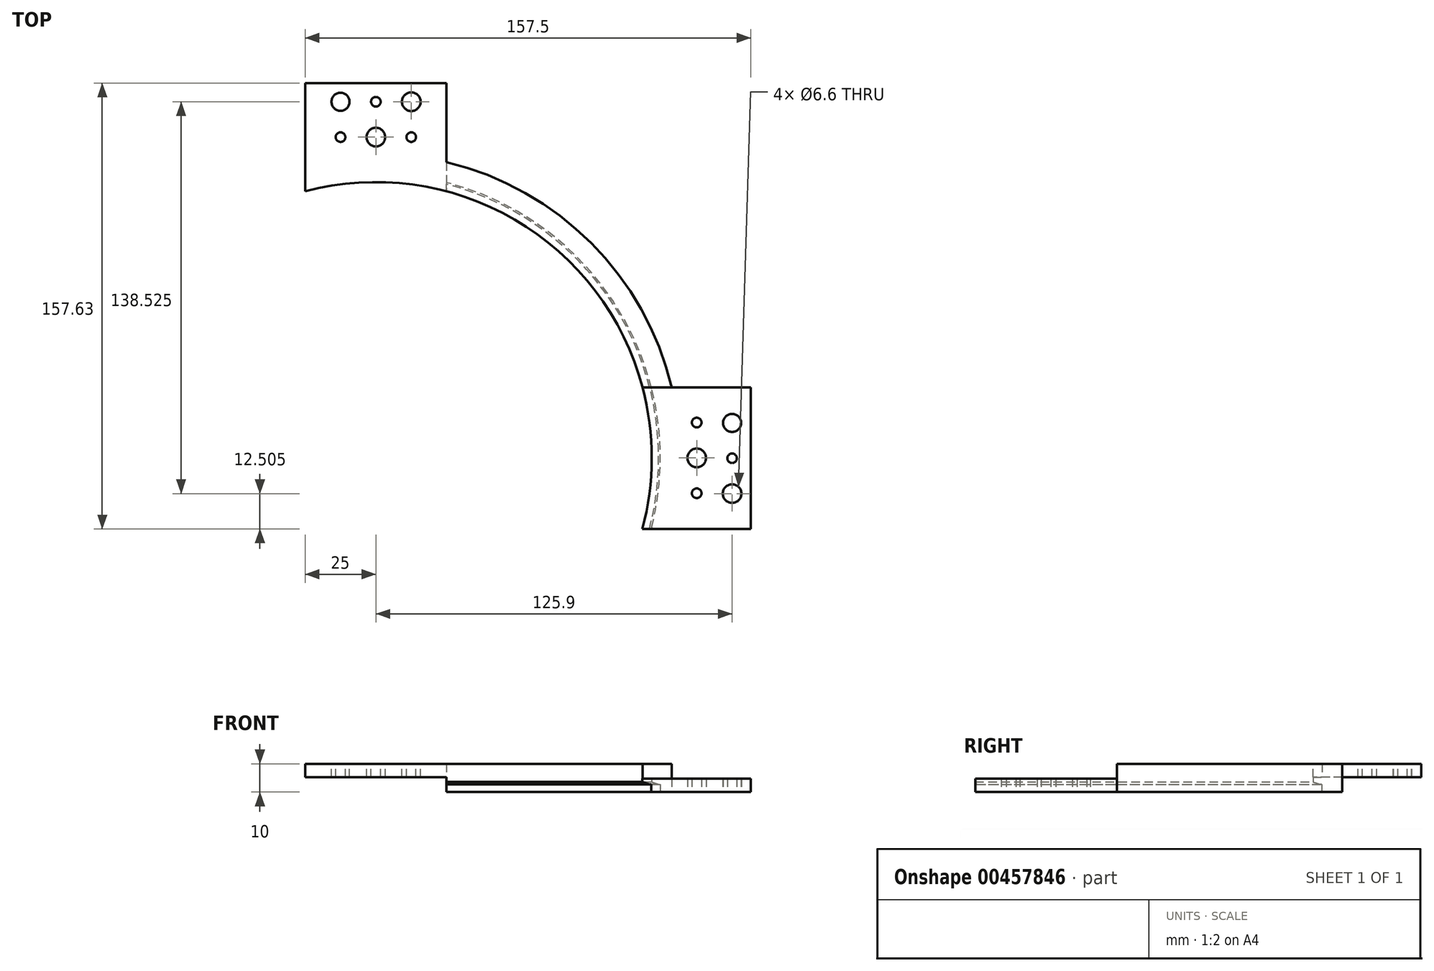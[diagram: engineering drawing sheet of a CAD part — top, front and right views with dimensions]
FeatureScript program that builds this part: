
annotation { "Feature Type Name" : "Feature", "Feature Type Description" : "" }
export const myFeature = defineFeature(function(context is Context, id is Id, definition is map)
    precondition{}
    {
        {
            var Q0;
            Q0=qCreatedBy(makeId("Top.planeOp"),FACE);
            var sketch = newSketch(context, id + "F0", { "sketchPlane" : qUnion([Q0])});
            skCircle(sketch, "E0", {"center": v(0, 0) * mm, "radius": 97.5 * mm});
            skCircle(sketch, "E1", {"center": v(0, 0) * mm, "radius": 107.5 * mm});
            skLineSegment(sketch, "E2", {"start": v(-97.5, 0) * mm, "end": v(-107.5, 0) * mm});
            skLineSegment(sketch, "E3", {"start": v(0, 97.5) * mm, "end": v(0, 107.5) * mm});
            skLineSegment(sketch, "E4", {"start": v(0, -97.5) * mm, "end": v(0, -107.5) * mm});
            skLineSegment(sketch, "E5.bottom", {"start": v(0, 97.5) * mm, "end": v(24.37, 97.5) * mm, "construction": true});
            skLineSegment(sketch, "E5.top", {"start": v(0, 132.5) * mm, "end": v(25, 132.5) * mm, "construction": true});
            skLineSegment(sketch, "E5.left", {"start": v(0, 97.5) * mm, "end": v(0, 132.5) * mm, "construction": true});
            skLineSegment(sketch, "E5.right", {"start": v(25, 97.5) * mm, "end": v(25, 132.5) * mm, "construction": true});
            skLineSegment(sketch, "E6.bottom", {"start": v(0, 132.5) * mm, "end": v(-25, 132.5) * mm, "construction": true});
            skLineSegment(sketch, "E6.top", {"start": v(0, 97.5) * mm, "end": v(-24.37, 97.5) * mm, "construction": true});
            skLineSegment(sketch, "E6.left", {"start": v(0, 132.5) * mm, "end": v(0, 97.5) * mm, "construction": true});
            skLineSegment(sketch, "E6.right", {"start": v(-25, 132.5) * mm, "end": v(-25, 97.5) * mm, "construction": true});
            skLineSegment(sketch, "E7.bottom", {"start": v(-25, 132.5) * mm, "end": v(25, 132.5) * mm});
            skLineSegment(sketch, "E7.top", {"start": v(-24.37, 97.5) * mm, "end": v(24.37, 97.5) * mm});
            skLineSegment(sketch, "E7.left", {"start": v(-25, 132.5) * mm, "end": v(-25, 97.5) * mm});
            skLineSegment(sketch, "E7.right", {"start": v(25, 132.5) * mm, "end": v(25, 97.5) * mm});
            skCircle(sketch, "E8", {"center": v(-12.5, 125.9) * mm, "radius": 3.2 * mm});
            skCircle(sketch, "E9", {"center": v(12.5, 125.9) * mm, "radius": 3.3 * mm});
            skLineSegment(sketch, "E10.top", {"start": v(97.48, -24.43) * mm, "end": v(97.48, -0.13) * mm, "construction": true});
            skLineSegment(sketch, "E11.left", {"start": v(97.48, 0.12) * mm, "end": v(97.48, 24.43) * mm, "construction": true});
            skLineSegment(sketch, "E12", {"start": v(0, 132.5) * mm, "end": v(0, 107.5) * mm});
            skLineSegment(sketch, "E13", {"start": v(-25, 97.5) * mm, "end": v(-25, 94.24) * mm});
            skLineSegment(sketch, "E14", {"start": v(25, 97.5) * mm, "end": v(25, 94.24) * mm});
            skArc(sketch, "E15", {"start": v(24.37, 97.5) * mm, "mid": v(0, 100.5) * mm, "end": v(-24.37, 97.5) * mm});
            skCircle(sketch, "E16", {"center": v(0, 113.4) * mm, "radius": 3.3 * mm});
            skCircle(sketch, "E17", {"center": v(12.5, 113.4) * mm, "radius": 1.7 * mm});
            skCircle(sketch, "E18", {"center": v(-12.5, 113.4) * mm, "radius": 1.7 * mm});
            skLineSegment(sketch, "E19", {"start": v(97.48, -0.13) * mm, "end": v(107.5, -0.13) * mm});
            skLineSegment(sketch, "E20.bottom", {"start": v(97.48, -0.13) * mm, "end": v(97.48, -24.43) * mm, "construction": true});
            skLineSegment(sketch, "E20.top", {"start": v(132.5, -0.13) * mm, "end": v(132.5, -25.13) * mm, "construction": true});
            skLineSegment(sketch, "E20.left", {"start": v(97.48, -0.13) * mm, "end": v(132.5, -0.13) * mm, "construction": true});
            skLineSegment(sketch, "E20.right", {"start": v(97.48, -25.13) * mm, "end": v(132.5, -25.13) * mm, "construction": true});
            skLineSegment(sketch, "E21.bottom", {"start": v(132.5, -0.13) * mm, "end": v(132.5, 24.87) * mm, "construction": true});
            skLineSegment(sketch, "E21.top", {"start": v(97.48, -0.13) * mm, "end": v(97.48, 24.43) * mm, "construction": true});
            skLineSegment(sketch, "E21.left", {"start": v(132.5, -0.13) * mm, "end": v(97.48, -0.13) * mm, "construction": true});
            skLineSegment(sketch, "E21.right", {"start": v(132.5, 24.87) * mm, "end": v(97.48, 24.87) * mm, "construction": true});
            skLineSegment(sketch, "E22.bottom", {"start": v(132.5, 24.87) * mm, "end": v(132.5, -25.13) * mm});
            skLineSegment(sketch, "E22.top", {"start": v(97.48, 24.43) * mm, "end": v(97.48, -24.43) * mm});
            skLineSegment(sketch, "E22.left", {"start": v(132.5, 24.87) * mm, "end": v(97.48, 24.87) * mm});
            skLineSegment(sketch, "E22.right", {"start": v(132.5, -25.13) * mm, "end": v(97.48, -25.13) * mm});
            skCircle(sketch, "E23", {"center": v(125.9, 12.37) * mm, "radius": 3.2 * mm});
            skCircle(sketch, "E24", {"center": v(125.9, -12.63) * mm, "radius": 3.3 * mm});
            skLineSegment(sketch, "E25", {"start": v(132.5, -0.13) * mm, "end": v(107.5, -0.13) * mm});
            skLineSegment(sketch, "E26", {"start": v(97.48, 24.87) * mm, "end": v(94.2, 24.87) * mm});
            skLineSegment(sketch, "E27", {"start": v(97.48, -25.13) * mm, "end": v(94.2, -25.13) * mm});
            skCircle(sketch, "E28", {"center": v(113.4, 0) * mm, "radius": 3.3 * mm});
            skCircle(sketch, "E29", {"center": v(113.4, -12.5) * mm, "radius": 1.7 * mm});
            skCircle(sketch, "E30", {"center": v(113.4, 12.5) * mm, "radius": 1.7 * mm});
            skArc(sketch, "E31.trimOffspring", {"start": v(-25, 97.34) * mm, "mid": v(-71.1, -71.02) * mm, "end": v(97.3, -25.13) * mm});
            skArc(sketch, "E32.trimOffspring", {"start": v(97.37, 24.87) * mm, "mid": v(71.1, 71.02) * mm, "end": v(25, 97.34) * mm});
            skArc(sketch, "E33.trimOffspring", {"start": v(97.48, -24.43) * mm, "mid": v(100.5, 0) * mm, "end": v(97.48, 24.43) * mm});
            skLineSegment(sketch, "E34", {"start": v(97.48, -24.43) * mm, "end": v(97.3, -25.13) * mm});
            skLineSegment(sketch, "E35", {"start": v(97.48, 24.43) * mm, "end": v(97.37, 24.87) * mm});
            skLineSegment(sketch, "E36", {"start": v(-25, 97.34) * mm, "end": v(-24.37, 97.5) * mm});
            skLineSegment(sketch, "E37", {"start": v(24.37, 97.5) * mm, "end": v(25, 97.34) * mm});
            skCircle(sketch, "E38", {"center": v(125.9, -0.13) * mm, "radius": 1.7 * mm});
            skCircle(sketch, "E39", {"center": v(0, 125.9) * mm, "radius": 1.7 * mm});
            skSolve(sketch);
        }
        {
            var Q0;
            {var subQ4=sQuery(id+"F0.wireOp",EDGE,"E14");Q0=makeQuery(id+"F0.imprint","IMPRINT",FACE,{"disambiguationData":[TD([[makeQuery(id+"F0.imprint","IMPRINT",EDGE,{"derivedFrom":subQ4}),1.0]])]});}
            var Q1;
            {var subQ7=sQuery(id+"F0.wireOp",EDGE,"E1");var subQ9=sQuery(id+"F0.wireOp",EDGE,"E22.left");var subQ10=makeQuery(id+"F0.imprint","INTERSECT",VERTEX,{"derivedFrom":[subQ7,subQ9]});Q1=makeQuery(id+"F0.imprint","IMPRINT",FACE,{"disambiguationData":[TD([[makeQuery(id+"F0.imprint","IMPRINT",EDGE,{"disambiguationData":[TD([[subQ10,-1.0]])],"derivedFrom":subQ7}),1.0]])]});}
            extrude(context, id + "F1", {"entities" : qUnion([Q0, Q1]), "depth" : 10 * mm});
        }
        {
            var Q0;
            Q0=makeQuery(id+"F1.opExtrude","CAP_FACE",FACE,{"disambiguationData":[OSD([sQuery(id+"F0.wireOp",EDGE,"E0"),sQuery(id+"F0.wireOp",EDGE,"E1"),sQuery(id+"F0.wireOp",EDGE,"E7.right"),sQuery(id+"F0.wireOp",EDGE,"E14"),sQuery(id+"F0.wireOp",EDGE,"E22.left"),sQuery(id+"F0.wireOp",EDGE,"E26")])],"isStart":false});
            var sketch = newSketch(context, id + "F2", { "sketchPlane" : qUnion([Q0])});
            skLineSegment(sketch, "E40.0.3", {"start": v(0, 100.5) * mm, "end": v(0, 100.5) * mm});
            skArc(sketch, "E41.0", {"start": v(24.37, 97.5) * mm, "mid": v(0, 100.5) * mm, "end": v(-24.37, 97.5) * mm});
            skLineSegment(sketch, "E42.0", {"start": v(0, 97.5) * mm, "end": v(0, 107.5) * mm});
            skLineSegment(sketch, "E43.0", {"start": v(-24.37, 97.5) * mm, "end": v(24.37, 97.5) * mm});
            skCircle(sketch, "E44.0", {"center": v(0, 0) * mm, "radius": 97.5 * mm});
            skLineSegment(sketch, "E45.0", {"start": v(24.37, 97.5) * mm, "end": v(25, 97.34) * mm});
            skLineSegment(sketch, "E46.0", {"start": v(25, 97.5) * mm, "end": v(25, 94.24) * mm});
            skLineSegment(sketch, "E47.0", {"start": v(25, 132.5) * mm, "end": v(25, 97.5) * mm});
            skLineSegment(sketch, "E48.0", {"start": v(-25, 97.5) * mm, "end": v(-25, 94.24) * mm});
            skLineSegment(sketch, "E49.0", {"start": v(-25, 97.34) * mm, "end": v(-24.37, 97.5) * mm});
            skLineSegment(sketch, "E50.0", {"start": v(-25, 132.5) * mm, "end": v(-25, 97.5) * mm});
            skCircle(sketch, "E51.0", {"center": v(0, 0) * mm, "radius": 107.5 * mm});
            skLineSegment(sketch, "E52.0", {"start": v(-25, 132.5) * mm, "end": v(25, 132.5) * mm});
            skCircle(sketch, "E53.0", {"center": v(12.5, 125.9) * mm, "radius": 3.3 * mm});
            skCircle(sketch, "E54.0.0", {"center": v(-12.5, 125.9) * mm, "radius": 3.2 * mm});
            skCircle(sketch, "E55.0", {"center": v(-12.5, 113.4) * mm, "radius": 1.7 * mm});
            skCircle(sketch, "E56.0", {"center": v(0, 113.4) * mm, "radius": 3.3 * mm});
            skCircle(sketch, "E57.0", {"center": v(12.5, 113.4) * mm, "radius": 1.7 * mm});
            skPoint(sketch, "E58.0", {"position": v(0, 125.9) * mm});
            skCircle(sketch, "E59.0", {"center": v(0, 125.9) * mm, "radius": 1.7 * mm});
            skSolve(sketch);
        }
        {
            var Q0;
            {var subQ6=sQuery(id+"F2.wireOp",EDGE,"E52.0");Q0=makeQuery(id+"F2.imprint","IMPRINT",FACE,{"disambiguationData":[TD([[makeQuery(id+"F2.imprint","IMPRINT",EDGE,{"derivedFrom":subQ6}),-1.0]])]});}
            var Q1;
            {var subQ0=sQuery(id+"F2.wireOp",EDGE,"E49.0");Q1=makeQuery(id+"F2.imprint","IMPRINT",FACE,{"disambiguationData":[TD([[makeQuery(id+"F2.imprint","IMPRINT",EDGE,{"derivedFrom":subQ0}),1.0]])]});}
            var Q2;
            {var subQ1=sQuery(id+"F2.wireOp",EDGE,"E45.0");Q2=makeQuery(id+"F2.imprint","IMPRINT",FACE,{"disambiguationData":[TD([[makeQuery(id+"F2.imprint","IMPRINT",EDGE,{"derivedFrom":subQ1}),1.0]])]});}
            var Q3;
            {var subQ1=sQuery(id+"F2.wireOp",EDGE,"E41.0");var subQ3=sQuery(id+"F2.wireOp",EDGE,"E42.0");var subQ4=makeQuery(id+"F2.imprint","INTERSECT",VERTEX,{"derivedFrom":[subQ1,subQ3]});Q3=makeQuery(id+"F2.imprint","IMPRINT",FACE,{"disambiguationData":[TD([[makeQuery(id+"F2.imprint","IMPRINT",EDGE,{"disambiguationData":[TD([[subQ4,1.0]])],"derivedFrom":subQ1}),1.0]])]});}
            var Q4;
            {var subQ1=sQuery(id+"F2.wireOp",EDGE,"E41.0");var subQ3=sQuery(id+"F2.wireOp",EDGE,"E42.0");var subQ4=makeQuery(id+"F2.imprint","INTERSECT",VERTEX,{"derivedFrom":[subQ1,subQ3]});Q4=makeQuery(id+"F2.imprint","IMPRINT",FACE,{"disambiguationData":[TD([[makeQuery(id+"F2.imprint","IMPRINT",EDGE,{"disambiguationData":[TD([[subQ4,-1.0]])],"derivedFrom":subQ1}),1.0]])]});}
            var Q5;
            {var subQ0=sQuery(id+"F2.wireOp",EDGE,"E49.0");Q5=makeQuery(id+"F2.imprint","IMPRINT",FACE,{"disambiguationData":[TD([[makeQuery(id+"F2.imprint","IMPRINT",EDGE,{"derivedFrom":subQ0}),-1.0]])]});}
            var Q6;
            {var subQ0=sQuery(id+"F2.wireOp",EDGE,"E45.0");Q6=makeQuery(id+"F2.imprint","IMPRINT",FACE,{"disambiguationData":[TD([[makeQuery(id+"F2.imprint","IMPRINT",EDGE,{"derivedFrom":subQ0}),-1.0]])]});}
            extrude(context, id + "F3", {"entities" : qUnion([Q0, Q1, Q2, Q3, Q4, Q5, Q6]), "operationType" : NewBodyOperationType.ADD, "oppositeDirection" : true, "depth" : 4.8 * mm});
        }
        {
            var Q0;
            {var subQ0=sQuery(id+"F0.wireOp",EDGE,"E26");var subQ4=sQuery(id+"F0.wireOp",EDGE,"E0");var subQ7=makeQuery(id+"F0.imprint","INTERSECT",VERTEX,{"derivedFrom":[subQ4,subQ0]});Q0=makeQuery(id+"F0.imprint","IMPRINT",FACE,{"disambiguationData":[TD([[makeQuery(id+"F0.imprint","IMPRINT",EDGE,{"disambiguationData":[TD([[subQ7,1.0]])],"derivedFrom":subQ0}),1.0]])]});}
            var Q1;
            {var subQ0=sQuery(id+"F0.wireOp",EDGE,"E22.top");var subQ3=sQuery(id+"F0.wireOp",EDGE,"E33.trimOffspring");var subQ5=makeQuery(id+"F0.imprint","INTERSECT",VERTEX,{"disambiguationData":[OD(1.0)],"derivedFrom":[subQ0,subQ3]});Q1=makeQuery(id+"F0.imprint","IMPRINT",FACE,{"disambiguationData":[TD([[makeQuery(id+"F0.imprint","IMPRINT",EDGE,{"disambiguationData":[TD([[subQ5,1.0]])],"derivedFrom":subQ3}),1.0]])]});}
            var Q2;
            {var subQ1=sQuery(id+"F0.wireOp",EDGE,"E22.top");var subQ5=sQuery(id+"F0.wireOp",EDGE,"E33.trimOffspring");var subQ6=makeQuery(id+"F0.imprint","INTERSECT",VERTEX,{"disambiguationData":[OD(1.0)],"derivedFrom":[subQ1,subQ5]});Q2=makeQuery(id+"F0.imprint","IMPRINT",FACE,{"disambiguationData":[TD([[makeQuery(id+"F0.imprint","IMPRINT",EDGE,{"disambiguationData":[TD([[subQ6,1.0]])],"derivedFrom":subQ5}),-1.0]])]});}
            var Q3;
            Q3=makeQuery(id+"F0.imprint","IMPRINT",FACE,{"disambiguationData":[TD([[makeQuery(id+"F0.imprint","IMPRINT",EDGE,{"derivedFrom":sQuery(id+"F0.wireOp",EDGE,"E23")}),-1.0]])]});
            var Q4;
            {var subQ0=sQuery(id+"F0.wireOp",EDGE,"E27");var subQ5=sQuery(id+"F0.wireOp",EDGE,"E0");var subQ7=makeQuery(id+"F0.imprint","INTERSECT",VERTEX,{"derivedFrom":[subQ5,subQ0]});Q4=makeQuery(id+"F0.imprint","IMPRINT",FACE,{"disambiguationData":[TD([[makeQuery(id+"F0.imprint","IMPRINT",EDGE,{"disambiguationData":[TD([[subQ7,1.0]])],"derivedFrom":subQ0}),-1.0]])]});}
            var Q5;
            {var subQ0=sQuery(id+"F0.wireOp",EDGE,"E22.top");var subQ3=sQuery(id+"F0.wireOp",EDGE,"E33.trimOffspring");var subQ5=makeQuery(id+"F0.imprint","INTERSECT",VERTEX,{"disambiguationData":[OD(0.0)],"derivedFrom":[subQ0,subQ3]});Q5=makeQuery(id+"F0.imprint","IMPRINT",FACE,{"disambiguationData":[TD([[makeQuery(id+"F0.imprint","IMPRINT",EDGE,{"disambiguationData":[TD([[subQ5,-1.0]])],"derivedFrom":subQ3}),1.0]])]});}
            var Q6;
            {var subQ1=sQuery(id+"F0.wireOp",EDGE,"E22.top");var subQ3=sQuery(id+"F0.wireOp",EDGE,"E33.trimOffspring");var subQ4=makeQuery(id+"F0.imprint","INTERSECT",VERTEX,{"disambiguationData":[OD(0.0)],"derivedFrom":[subQ1,subQ3]});Q6=makeQuery(id+"F0.imprint","IMPRINT",FACE,{"disambiguationData":[TD([[makeQuery(id+"F0.imprint","IMPRINT",EDGE,{"disambiguationData":[TD([[subQ4,-1.0]])],"derivedFrom":subQ3}),-1.0]])]});}
            var Q7;
            Q7=makeQuery(id+"F0.imprint","IMPRINT",FACE,{"disambiguationData":[TD([[makeQuery(id+"F0.imprint","IMPRINT",EDGE,{"derivedFrom":sQuery(id+"F0.wireOp",EDGE,"E24")}),-1.0]])]});
            extrude(context, id + "F4", {"entities" : qUnion([Q0, Q1, Q2, Q3, Q4, Q5, Q6, Q7]), "operationType" : NewBodyOperationType.ADD, "depth" : 4.8 * mm});
        }
        {
            var Q0;
            {var subQ0=sQuery(id+"F0.wireOp",EDGE,"E13");var subQ4=sQuery(id+"F0.wireOp",EDGE,"E0");var subQ7=makeQuery(id+"F0.imprint","INTERSECT",VERTEX,{"derivedFrom":[subQ4,subQ0]});Q0=makeQuery(id+"F0.imprint","IMPRINT",FACE,{"disambiguationData":[TD([[makeQuery(id+"F0.imprint","IMPRINT",EDGE,{"disambiguationData":[TD([[subQ7,1.0]])],"derivedFrom":subQ0}),1.0]])]});}
            var Q1;
            {var subQ0=sQuery(id+"F0.wireOp",EDGE,"E7.top");var subQ3=sQuery(id+"F0.wireOp",EDGE,"E15");var subQ5=makeQuery(id+"F0.imprint","INTERSECT",VERTEX,{"disambiguationData":[OD(1.0)],"derivedFrom":[subQ0,subQ3]});Q1=makeQuery(id+"F0.imprint","IMPRINT",FACE,{"disambiguationData":[TD([[makeQuery(id+"F0.imprint","IMPRINT",EDGE,{"disambiguationData":[TD([[subQ5,1.0]])],"derivedFrom":subQ3}),1.0]])]});}
            var Q2;
            {var subQ0=sQuery(id+"F0.wireOp",EDGE,"E7.top");var subQ3=sQuery(id+"F0.wireOp",EDGE,"E15");var subQ5=makeQuery(id+"F0.imprint","INTERSECT",VERTEX,{"disambiguationData":[OD(0.0)],"derivedFrom":[subQ0,subQ3]});Q2=makeQuery(id+"F0.imprint","IMPRINT",FACE,{"disambiguationData":[TD([[makeQuery(id+"F0.imprint","IMPRINT",EDGE,{"disambiguationData":[TD([[subQ5,-1.0]])],"derivedFrom":subQ3}),1.0]])]});}
            var Q3;
            {var subQ0=sQuery(id+"F0.wireOp",EDGE,"E14");var subQ4=sQuery(id+"F0.wireOp",EDGE,"E0");var subQ7=makeQuery(id+"F0.imprint","INTERSECT",VERTEX,{"derivedFrom":[subQ4,subQ0]});Q3=makeQuery(id+"F0.imprint","IMPRINT",FACE,{"disambiguationData":[TD([[makeQuery(id+"F0.imprint","IMPRINT",EDGE,{"disambiguationData":[TD([[subQ7,1.0]])],"derivedFrom":subQ0}),-1.0]])]});}
            var Q4;
            {var subQ5=sQuery(id+"F0.wireOp",EDGE,"E32.trimOffspring");Q4=makeQuery(id+"F0.imprint","IMPRINT",FACE,{"disambiguationData":[TD([[makeQuery(id+"F0.imprint","IMPRINT",EDGE,{"derivedFrom":subQ5}),1.0]])]});}
            var Q5;
            {var subQ0=sQuery(id+"F0.wireOp",EDGE,"E26");var subQ4=sQuery(id+"F0.wireOp",EDGE,"E0");var subQ7=makeQuery(id+"F0.imprint","INTERSECT",VERTEX,{"derivedFrom":[subQ4,subQ0]});Q5=makeQuery(id+"F0.imprint","IMPRINT",FACE,{"disambiguationData":[TD([[makeQuery(id+"F0.imprint","IMPRINT",EDGE,{"disambiguationData":[TD([[subQ7,1.0]])],"derivedFrom":subQ0}),1.0]])]});}
            var Q6;
            {var subQ0=sQuery(id+"F0.wireOp",EDGE,"E22.top");var subQ3=sQuery(id+"F0.wireOp",EDGE,"E33.trimOffspring");var subQ5=makeQuery(id+"F0.imprint","INTERSECT",VERTEX,{"disambiguationData":[OD(1.0)],"derivedFrom":[subQ0,subQ3]});Q6=makeQuery(id+"F0.imprint","IMPRINT",FACE,{"disambiguationData":[TD([[makeQuery(id+"F0.imprint","IMPRINT",EDGE,{"disambiguationData":[TD([[subQ5,1.0]])],"derivedFrom":subQ3}),1.0]])]});}
            var Q7;
            {var subQ0=sQuery(id+"F0.wireOp",EDGE,"E27");var subQ5=sQuery(id+"F0.wireOp",EDGE,"E0");var subQ7=makeQuery(id+"F0.imprint","INTERSECT",VERTEX,{"derivedFrom":[subQ5,subQ0]});Q7=makeQuery(id+"F0.imprint","IMPRINT",FACE,{"disambiguationData":[TD([[makeQuery(id+"F0.imprint","IMPRINT",EDGE,{"disambiguationData":[TD([[subQ7,1.0]])],"derivedFrom":subQ0}),-1.0]])]});}
            var Q8;
            {var subQ0=sQuery(id+"F0.wireOp",EDGE,"E22.top");var subQ3=sQuery(id+"F0.wireOp",EDGE,"E33.trimOffspring");var subQ5=makeQuery(id+"F0.imprint","INTERSECT",VERTEX,{"disambiguationData":[OD(0.0)],"derivedFrom":[subQ0,subQ3]});Q8=makeQuery(id+"F0.imprint","IMPRINT",FACE,{"disambiguationData":[TD([[makeQuery(id+"F0.imprint","IMPRINT",EDGE,{"disambiguationData":[TD([[subQ5,-1.0]])],"derivedFrom":subQ3}),1.0]])]});}
            extrude(context, id + "F5", {"entities" : qUnion([Q0, Q1, Q2, Q3, Q4, Q5, Q6, Q7, Q8]), "operationType" : NewBodyOperationType.REMOVE, "depth" : 2.75 * mm});
        }
        {
            var Q0;
            Q0=makeQuery(id+"F4.opExtrude","SWEPT_FACE",FACE,{"disambiguationData":[OSD([sQuery(id+"F0.wireOp",EDGE,"E22.right"),sQuery(id+"F0.wireOp",EDGE,"E27")])]});
            var sketch = newSketch(context, id + "F6", { "sketchPlane" : qUnion([Q0])});
            skLineSegment(sketch, "E60", {"start": v(97.3, 2.75) * mm, "end": v(96.7, 2.75) * mm});
            skLineSegment(sketch, "E61", {"start": v(96.7, 2.75) * mm, "end": v(94.2, 3.55) * mm});
            skLineSegment(sketch, "E62", {"start": v(94.2, 3.55) * mm, "end": v(94.2, 2.75) * mm});
            skLineSegment(sketch, "E63", {"start": v(94.2, 2.75) * mm, "end": v(96.7, 2.75) * mm});
            skSolve(sketch);
        }
        {
            var Q0;
            Q0=qCreatedBy(makeId("Right.planeOp"),FACE);
            var sketch = newSketch(context, id + "F7", { "sketchPlane" : qUnion([Q0])});
            skLineSegment(sketch, "E64", {"start": v(0, 0) * mm, "end": v(0, 32.62) * mm, "construction": true});
            skSolve(sketch);
        }
        {
            var Q0;
            Q0=makeQuery(id+"F6.imprint","IMPRINT",FACE,{"disambiguationData":[TD([[makeQuery(id+"F6.imprint","IMPRINT",EDGE,{"derivedFrom":sQuery(id+"F6.wireOp",EDGE,"E61")}),1.0]])]});
            var Q1;
            Q1=sQuery(id+"F7.wireOp",EDGE,"E64");
            revolve(context, id + "F8", {"operationType" : NewBodyOperationType.REMOVE, "entities" : qUnion([Q0]), "axis" : qUnion([Q1]), "revolveType" : RevolveType.FULL, "oppositeDirection" : true});
        }
    });
